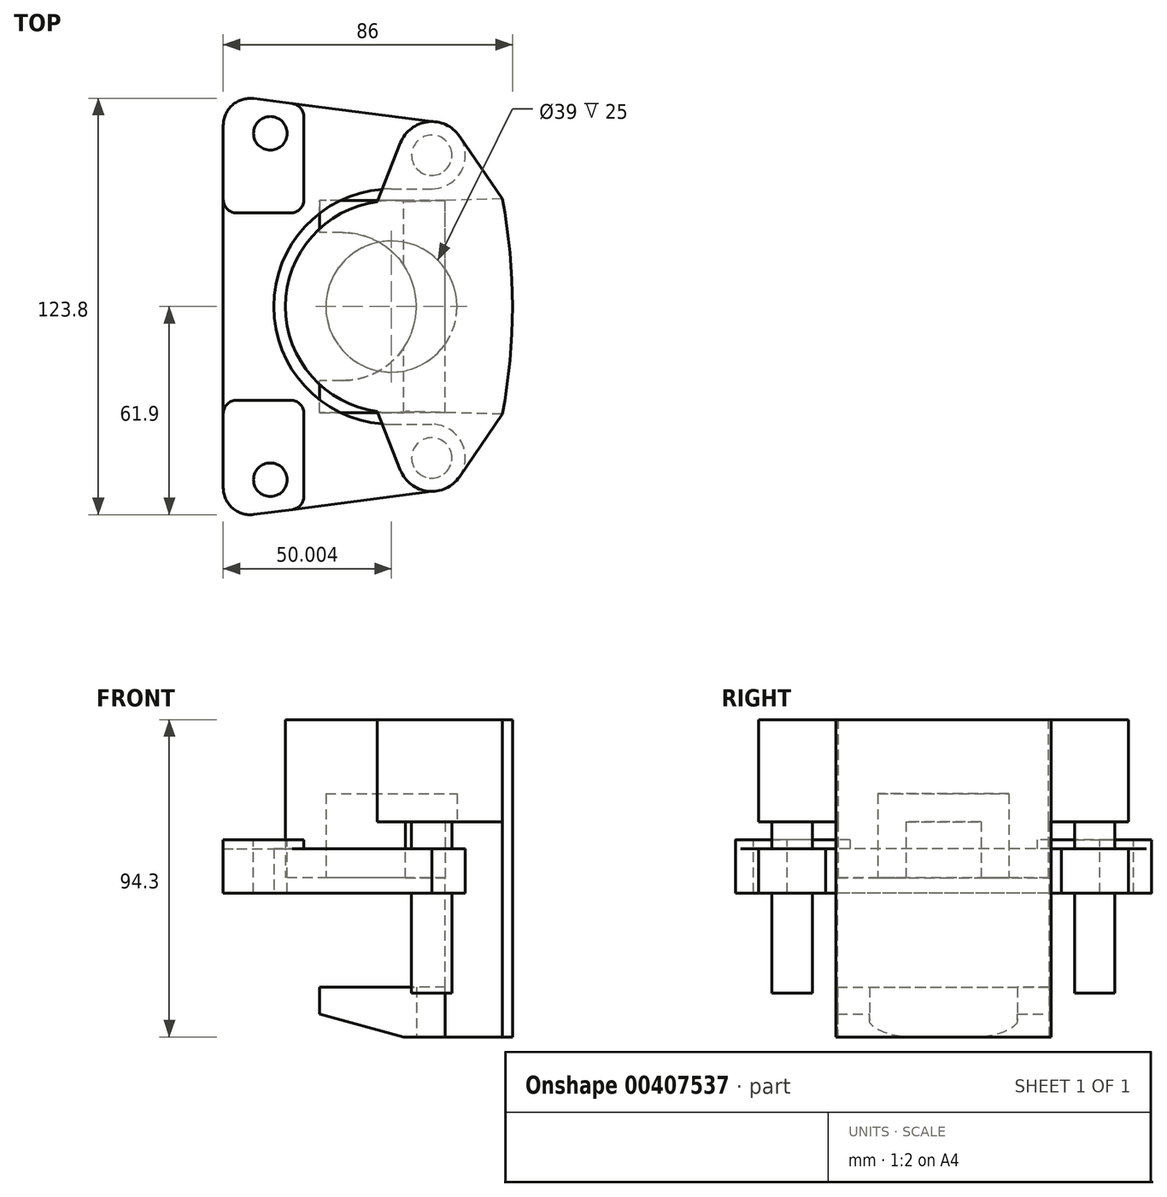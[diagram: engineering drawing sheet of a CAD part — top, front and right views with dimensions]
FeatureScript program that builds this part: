
annotation { "Feature Type Name" : "Feature", "Feature Type Description" : "" }
export const myFeature = defineFeature(function(context is Context, id is Id, definition is map)
    precondition{}
    {
        {
            var Q0;
            Q0=qCreatedBy(makeId("Top.planeOp"),FACE);
            var sketch = newSketch(context, id + "F0", { "sketchPlane" : qUnion([Q0])});
            skLineSegment(sketch, "E0", {"start": v(-41.04, 0) * mm, "end": v(-41.04, -63) * mm});
            skLineSegment(sketch, "E1", {"start": v(-41.04, -63) * mm, "end": v(20.96, -55) * mm});
            skLineSegment(sketch, "E2", {"start": v(20.96, -55) * mm, "end": v(20.96, -55) * mm});
            skArc(sketch, "E3", {"start": v(20.96, -55) * mm, "mid": v(30.96, -45) * mm, "end": v(20.96, -35) * mm});
            skLineSegment(sketch, "E4", {"start": v(20.96, -55) * mm, "end": v(20.96, -22.35) * mm, "construction": true});
            skLineSegment(sketch, "E5", {"start": v(-26.04, 0) * mm, "end": v(-26.04, 35.16) * mm, "construction": true});
            skArc(sketch, "E6", {"start": v(-26.04, 0) * mm, "mid": v(-15.79, -24.75) * mm, "end": v(8.96, -35) * mm});
            skLineSegment(sketch, "E7", {"start": v(8.96, -35) * mm, "end": v(20.96, -35) * mm});
            skLineSegment(sketch, "E8.MirrorCS", {"start": v(-41.04, 0) * mm, "end": v(-41.04, 63) * mm});
            skLineSegment(sketch, "E9.MirrorCS", {"start": v(-41.04, 63) * mm, "end": v(20.96, 55) * mm});
            skArc(sketch, "E10.MirrorCS", {"start": v(20.96, 55) * mm, "mid": v(30.96, 45) * mm, "end": v(20.96, 35) * mm});
            skLineSegment(sketch, "E11.MirrorCS", {"start": v(8.96, 35) * mm, "end": v(20.96, 35) * mm});
            skArc(sketch, "E12.MirrorCS", {"start": v(-26.04, 0) * mm, "mid": v(-15.79, 24.75) * mm, "end": v(8.96, 35) * mm});
            skSolve(sketch);
        }
        {
            var Q0;
            Q0=qSketchRegion(id+"F0",true);
            extrude(context, id + "F1", {"entities" : qUnion([Q0]), "depth" : 13.2 * mm, "offsetDistance" : 25 * mm});
        }
        {
            var Q0;
            Q0=makeQuery(id+"F1.opExtrude","SWEPT_EDGE",EDGE,{"disambiguationData":[OSD([sQuery(id+"F0.wireOp",EDGE,"E0"),sQuery(id+"F0.wireOp",EDGE,"E1")])]});
            var Q1;
            Q1=makeQuery(id+"F1.opExtrude","SWEPT_EDGE",EDGE,{"disambiguationData":[OSD([sQuery(id+"F0.wireOp",EDGE,"E8.MirrorCS"),sQuery(id+"F0.wireOp",EDGE,"E9.MirrorCS")])]});
            fillet(context, id + "F2", {"entities" : qUnion([Q0, Q1]), "tangentPropagation" : true, "radius" : 8 * mm, "defaultsChanged" : false, "vertexSettings" : [], "allowEdgeOverflow" : false});
        }
        {
            var Q0;
            Q0=makeQuery(id+"F1.opExtrude","CAP_FACE",FACE,{"disambiguationData":[OSD([sQuery(id+"F0.wireOp",EDGE,"E0"),sQuery(id+"F0.wireOp",EDGE,"E1"),sQuery(id+"F0.wireOp",EDGE,"E3"),sQuery(id+"F0.wireOp",EDGE,"E6"),sQuery(id+"F0.wireOp",EDGE,"E7"),sQuery(id+"F0.wireOp",EDGE,"E8.MirrorCS"),sQuery(id+"F0.wireOp",EDGE,"E9.MirrorCS"),sQuery(id+"F0.wireOp",EDGE,"E10.MirrorCS"),sQuery(id+"F0.wireOp",EDGE,"E11.MirrorCS"),sQuery(id+"F0.wireOp",EDGE,"E12.MirrorCS")])],"isStart":false});
            var sketch = newSketch(context, id + "F3", { "sketchPlane" : qUnion([Q0])});
            skLineSegment(sketch, "E13", {"start": v(-41.04, 53.9) * mm, "end": v(-41.04, 31.84) * mm});
            skLineSegment(sketch, "E14", {"start": v(-37.04, 27.84) * mm, "end": v(-21.04, 27.84) * mm});
            skLineSegment(sketch, "E15", {"start": v(-17.04, 31.84) * mm, "end": v(-17.04, 56.39) * mm});
            skLineSegment(sketch, "E16", {"start": v(-20.52, 60.35) * mm, "end": v(-32.01, 61.84) * mm});
            skArc(sketch, "E17", {"start": v(-32.01, 61.84) * mm, "mid": v(-38.32, 59.9) * mm, "end": v(-41.04, 53.9) * mm});
            skPoint(sketch, "E18.visualSharp", {"position": v(-17.04, 27.84) * mm});
            skArc(sketch, "E18.filletArc", {"start": v(-21.04, 27.84) * mm, "mid": v(-18.2, 29) * mm, "end": v(-17.04, 31.84) * mm});
            skPoint(sketch, "E19.visualSharp", {"position": v(-17.04, 59.9) * mm});
            skArc(sketch, "E19.filletArc", {"start": v(-17.04, 56.39) * mm, "mid": v(-18.03, 59.03) * mm, "end": v(-20.52, 60.35) * mm});
            skPoint(sketch, "E20.visualSharp", {"position": v(-41.04, 27.84) * mm});
            skArc(sketch, "E20.filletArc", {"start": v(-41.04, 31.84) * mm, "mid": v(-39.86, 29) * mm, "end": v(-37.04, 27.84) * mm});
            skLineSegment(sketch, "E21.MirrorCS", {"start": v(-20.52, -60.35) * mm, "end": v(-32.01, -61.84) * mm});
            skArc(sketch, "E22.MirrorCS", {"start": v(-21.04, -27.84) * mm, "mid": v(-18.2, -29) * mm, "end": v(-17.04, -31.84) * mm});
            skArc(sketch, "E23.MirrorCS", {"start": v(-41.04, -31.84) * mm, "mid": v(-39.86, -29) * mm, "end": v(-37.04, -27.84) * mm});
            skArc(sketch, "E24.MirrorCS", {"start": v(-32.01, -61.84) * mm, "mid": v(-38.32, -59.9) * mm, "end": v(-41.04, -53.9) * mm});
            skArc(sketch, "E25.MirrorCS", {"start": v(-17.04, -56.39) * mm, "mid": v(-18.03, -59.03) * mm, "end": v(-20.52, -60.35) * mm});
            skLineSegment(sketch, "E26.MirrorCS", {"start": v(-37.04, -27.84) * mm, "end": v(-21.04, -27.84) * mm});
            skLineSegment(sketch, "E27.MirrorCS", {"start": v(-41.04, -53.9) * mm, "end": v(-41.04, -31.84) * mm});
            skLineSegment(sketch, "E28.MirrorCS", {"start": v(-17.04, -31.84) * mm, "end": v(-17.04, -56.39) * mm});
            skPoint(sketch, "E29.MirrorP", {"position": v(-17.04, -59.9) * mm});
            skPoint(sketch, "E30.MirrorP", {"position": v(-17.04, -27.84) * mm});
            skPoint(sketch, "E31.MirrorP", {"position": v(-41.04, -27.84) * mm});
            skSolve(sketch);
        }
        {
            var Q0;
            Q0=qSketchRegion(id+"F3",true);
            extrude(context, id + "F4", {"entities" : qUnion([Q0]), "operationType" : NewBodyOperationType.ADD, "depth" : 2.6 * mm, "offsetDistance" : 25 * mm});
        }
        {
            var Q0;
            Q0=makeQuery(id+"F4.opExtrude","CAP_FACE",FACE,{"disambiguationData":[OSD([sQuery(id+"F3.wireOp",EDGE,"E13"),sQuery(id+"F3.wireOp",EDGE,"E14"),sQuery(id+"F3.wireOp",EDGE,"E15"),sQuery(id+"F3.wireOp",EDGE,"E16"),sQuery(id+"F3.wireOp",EDGE,"E17"),sQuery(id+"F3.wireOp",EDGE,"E18.filletArc"),sQuery(id+"F3.wireOp",EDGE,"E19.filletArc"),sQuery(id+"F3.wireOp",EDGE,"E20.filletArc")])],"isStart":false});
            var sketch = newSketch(context, id + "F5", { "sketchPlane" : qUnion([Q0])});
            skCircle(sketch, "E32", {"center": v(-27.04, 51.5) * mm, "radius": 5 * mm});
            skCircle(sketch, "E33.MirrorC", {"center": v(-27.04, -51.5) * mm, "radius": 5 * mm});
            skSolve(sketch);
        }
        {
            var Q0;
            Q0=qSketchRegion(id+"F5",true);
            extrude(context, id + "F6", {"entities" : qUnion([Q0]), "operationType" : NewBodyOperationType.REMOVE, "endBound" : BoundingType.THROUGH_ALL, "oppositeDirection" : true, "depth" : 25 * mm, "offsetDistance" : 25 * mm});
        }
        {
            var Q0;
            Q0=makeQuery(id+"F1.opExtrude","CAP_FACE",FACE,{"disambiguationData":[OSD([sQuery(id+"F0.wireOp",EDGE,"E0"),sQuery(id+"F0.wireOp",EDGE,"E1"),sQuery(id+"F0.wireOp",EDGE,"E3"),sQuery(id+"F0.wireOp",EDGE,"E6"),sQuery(id+"F0.wireOp",EDGE,"E7"),sQuery(id+"F0.wireOp",EDGE,"E8.MirrorCS"),sQuery(id+"F0.wireOp",EDGE,"E9.MirrorCS"),sQuery(id+"F0.wireOp",EDGE,"E10.MirrorCS"),sQuery(id+"F0.wireOp",EDGE,"E11.MirrorCS"),sQuery(id+"F0.wireOp",EDGE,"E12.MirrorCS")])],"isStart":false});
            var sketch = newSketch(context, id + "F7", { "sketchPlane" : qUnion([Q0])});
            skCircle(sketch, "E34", {"center": v(20.96, 45) * mm, "radius": 6 * mm});
            skCircle(sketch, "E35.MirrorC", {"center": v(20.96, -45) * mm, "radius": 6 * mm});
            skSolve(sketch);
        }
        {
            var Q0;
            Q0 = qSketchRegion(id + "F7", true);
            extrude(context, id + "F8", {"entities" : qUnion([Q0]), "operationType" : NewBodyOperationType.REMOVE, "oppositeDirection" : true, "depth" : 25 * mm, "offsetDistance" : 25 * mm});
        }
        {
            var Q0;
            Q0=qCreatedBy(makeId("Top.planeOp"),FACE);
            var sketch = newSketch(context, id + "F9", { "sketchPlane" : qUnion([Q0])});
            skCircle(sketch, "E36", {"center": v(8.96, 0) * mm, "radius": 31.5 * mm});
            skSolve(sketch);
        }
        {
            var Q0;
            Q0 = qSketchRegion(id + "F9", true);
            extrude(context, id + "F10", {"entities" : qUnion([Q0]), "depth" : 51.5 * mm, "offsetDistance" : 25 * mm, "hasSecondDirection" : true, "secondDirectionOppositeDirection" : false, "secondDirectionDepth" : 4.5 * mm});
        }
        {
            var Q0;
            Q0=makeQuery(id+"F10.opExtrude","CAP_FACE",FACE,{"disambiguationData":[OSD([sQuery(id+"F9.wireOp",EDGE,"E36")])],"isStart":false});
            var sketch = newSketch(context, id + "F11", { "sketchPlane" : qUnion([Q0])});
            skCircle(sketch, "E37", {"center": v(20.96, -45) * mm, "radius": 10 * mm});
            skLineSegment(sketch, "E38", {"start": v(11.66, -48.66) * mm, "end": v(4.8, -31.22) * mm});
            skArc(sketch, "E39", {"start": v(41.96, -32) * mm, "mid": v(44.21, -16.07) * mm, "end": v(44.96, 0) * mm});
            skLineSegment(sketch, "E40", {"start": v(-22.54, 0) * mm, "end": v(40.46, 0) * mm, "construction": true});
            skPoint(sketch, "E41", {"position": v(8.96, 0) * mm});
            skLineSegment(sketch, "E42", {"start": v(41.96, -32) * mm, "end": v(29.22, -50.64) * mm});
            skCircle(sketch, "E43.MirrorC", {"center": v(20.96, 45) * mm, "radius": 10 * mm});
            skLineSegment(sketch, "E44.MirrorCS", {"start": v(11.66, 48.66) * mm, "end": v(4.8, 31.22) * mm});
            skLineSegment(sketch, "E45.MirrorCS", {"start": v(41.96, 32) * mm, "end": v(29.22, 50.64) * mm});
            skArc(sketch, "E46.MirrorCS", {"start": v(41.96, 32) * mm, "mid": v(44.21, 16.07) * mm, "end": v(44.96, 0) * mm});
            skLineSegment(sketch, "E47", {"start": v(4.8, -31.22) * mm, "end": v(4.8, 0) * mm});
            skLineSegment(sketch, "E48", {"start": v(4.8, 0) * mm, "end": v(4.8, 31.22) * mm});
            skSolve(sketch);
        }
        {
            var Q0;
            Q0 = qSketchRegion(id + "F11", true);
            var Q1;
            Q1=makeQuery(id+"F1.opExtrude","CAP_FACE",FACE,{"disambiguationData":[OSD([sQuery(id+"F0.wireOp",EDGE,"E0"),sQuery(id+"F0.wireOp",EDGE,"E1"),sQuery(id+"F0.wireOp",EDGE,"E3"),sQuery(id+"F0.wireOp",EDGE,"E6"),sQuery(id+"F0.wireOp",EDGE,"E7"),sQuery(id+"F0.wireOp",EDGE,"E8.MirrorCS"),sQuery(id+"F0.wireOp",EDGE,"E9.MirrorCS"),sQuery(id+"F0.wireOp",EDGE,"E10.MirrorCS"),sQuery(id+"F0.wireOp",EDGE,"E11.MirrorCS"),sQuery(id+"F0.wireOp",EDGE,"E12.MirrorCS")])],"isStart":false});
            extrude(context, id + "F12", {"entities" : qUnion([Q0]), "operationType" : NewBodyOperationType.ADD, "endBound" : BoundingType.UP_TO_SURFACE, "oppositeDirection" : true, "depth" : 25 * mm, "endBoundEntityFace" : qUnion([Q1]), "hasOffset" : true, "offsetDistance" : 8 * mm});
        }
        {
            var Q0;
            Q0=makeQuery(id+"F10.opExtrude","CAP_FACE",FACE,{"disambiguationData":[OSD([sQuery(id+"F9.wireOp",EDGE,"E36")])],"isStart":true});
            var sketch = newSketch(context, id + "F13", { "sketchPlane" : qUnion([Q0])});
            skCircle(sketch, "E49", {"center": v(8.96, 0) * mm, "radius": 19.5 * mm});
            skSolve(sketch);
        }
        {
            var Q0;
            Q0 = qSketchRegion(id + "F13", true);
            extrude(context, id + "F14", {"entities" : qUnion([Q0]), "operationType" : NewBodyOperationType.REMOVE, "oppositeDirection" : true, "depth" : 25 * mm, "offsetDistance" : 25 * mm});
        }
        {
            var Q0;
            Q0=makeQuery(id+"F12.opExtrude","CAP_FACE",FACE,{"disambiguationData":[OSD([sQuery(id+"F11.wireOp",EDGE,"E37"),sQuery(id+"F11.wireOp",EDGE,"E38"),sQuery(id+"F11.wireOp",EDGE,"E39"),sQuery(id+"F11.wireOp",EDGE,"E42"),sQuery(id+"F11.wireOp",EDGE,"E43.MirrorC"),sQuery(id+"F11.wireOp",EDGE,"E44.MirrorCS"),sQuery(id+"F11.wireOp",EDGE,"E45.MirrorCS"),sQuery(id+"F11.wireOp",EDGE,"E46.MirrorCS"),sQuery(id+"F11.wireOp",EDGE,"E47"),sQuery(id+"F11.wireOp",EDGE,"E48")])],"isStart":false});
            var sketch = newSketch(context, id + "F15", { "sketchPlane" : qUnion([Q0])});
            skCircle(sketch, "E50", {"center": v(20.96, -45) * mm, "radius": 6 * mm});
            skCircle(sketch, "E51.MirrorC", {"center": v(20.96, 45) * mm, "radius": 6 * mm});
            skSolve(sketch);
        }
        {
            var Q0;
            Q0 = qSketchRegion(id + "F15", true);
            extrude(context, id + "F16", {"entities" : qUnion([Q0]), "operationType" : NewBodyOperationType.ADD, "depth" : 51 * mm, "offsetDistance" : 25 * mm});
        }
        {
            var Q0;
            Q0=makeQuery(id+"F12.opExtrude","CAP_FACE",FACE,{"disambiguationData":[OSD([sQuery(id+"F11.wireOp",EDGE,"E37"),sQuery(id+"F11.wireOp",EDGE,"E38"),sQuery(id+"F11.wireOp",EDGE,"E39"),sQuery(id+"F11.wireOp",EDGE,"E42"),sQuery(id+"F11.wireOp",EDGE,"E43.MirrorC"),sQuery(id+"F11.wireOp",EDGE,"E44.MirrorCS"),sQuery(id+"F11.wireOp",EDGE,"E45.MirrorCS"),sQuery(id+"F11.wireOp",EDGE,"E46.MirrorCS"),sQuery(id+"F11.wireOp",EDGE,"E47"),sQuery(id+"F11.wireOp",EDGE,"E48")])],"isStart":false});
            var sketch = newSketch(context, id + "F17", { "sketchPlane" : qUnion([Q0])});
            skArc(sketch, "E52", {"start": v(41.96, -32) * mm, "mid": v(44.21, -16.07) * mm, "end": v(44.96, 0) * mm});
            skLineSegment(sketch, "E53", {"start": v(41.96, -32) * mm, "end": v(13.13, -31.22) * mm});
            skLineSegment(sketch, "E54", {"start": v(13.13, -31.22) * mm, "end": v(13.13, -31.22) * mm});
            skLineSegment(sketch, "E55", {"start": v(13.13, -31.22) * mm, "end": v(32.09, 0) * mm});
            skLineSegment(sketch, "E56.MirrorCS", {"start": v(13.13, 31.22) * mm, "end": v(32.09, 0) * mm});
            skLineSegment(sketch, "E57.MirrorCS", {"start": v(41.96, 32) * mm, "end": v(13.13, 31.22) * mm});
            skArc(sketch, "E58.MirrorCS", {"start": v(41.96, 32) * mm, "mid": v(44.21, 16.07) * mm, "end": v(44.96, 0) * mm});
            skSolve(sketch);
        }
        {
            var Q0;
            Q0 = qSketchRegion(id + "F17", true);
            var Q1;
            Q1=makeQuery(id+"F10.opExtrude","CAP_FACE",FACE,{"disambiguationData":[OSD([sQuery(id+"F9.wireOp",EDGE,"E36")])],"isStart":true});
            extrude(context, id + "F18", {"entities" : qUnion([Q0]), "operationType" : NewBodyOperationType.ADD, "endBound" : BoundingType.UP_TO_SURFACE, "depth" : 25 * mm, "endBoundEntityFace" : qUnion([Q1]), "offsetDistance" : 25 * mm});
        }
        {
            var Q0;
            {var subQ0=sQuery(id+"F11.wireOp",EDGE,"E46.MirrorCS");var subQ1=sQuery(id+"F11.wireOp",EDGE,"E39");var subQ2=sQuery(id+"F11.wireOp",EDGE,"E38");var subQ3=sQuery(id+"F11.wireOp",EDGE,"E37");var subQ4=sQuery(id+"F11.wireOp",EDGE,"E42");Q0=makeQuery(id+"F18.boolean.opBoolean","SPLIT",FACE,{"disambiguationData":[TD([makeQuery(id+"F12.opExtrude","SWEPT_FACE",FACE,{"disambiguationData":[OSD([subQ3])]})])],"derivedFrom":makeQuery(id+"F12.opExtrude","CAP_FACE",FACE,{"disambiguationData":[OSD([subQ3,subQ2,subQ1,subQ4,sQuery(id+"F11.wireOp",EDGE,"E43.MirrorC"),sQuery(id+"F11.wireOp",EDGE,"E44.MirrorCS"),sQuery(id+"F11.wireOp",EDGE,"E45.MirrorCS"),subQ0,sQuery(id+"F11.wireOp",EDGE,"E47"),sQuery(id+"F11.wireOp",EDGE,"E48")])],"isStart":false})});}
            var sketch = newSketch(context, id + "F19", { "sketchPlane" : qUnion([Q0])});
            skArc(sketch, "E59", {"start": v(41.96, -32) * mm, "mid": v(44.21, -16.07) * mm, "end": v(44.96, 0) * mm});
            skLineSegment(sketch, "E60", {"start": v(41.96, -32) * mm, "end": v(24.97, -31.54) * mm});
            skArc(sketch, "E61.MirrorCS", {"start": v(41.96, 32) * mm, "mid": v(44.21, 16.07) * mm, "end": v(44.96, 0) * mm});
            skLineSegment(sketch, "E62.MirrorCS", {"start": v(41.96, 32) * mm, "end": v(24.97, 31.54) * mm});
            skLineSegment(sketch, "E63", {"start": v(24.97, 31.54) * mm, "end": v(24.97, -31.54) * mm});
            skSolve(sketch);
        }
        {
            var Q0;
            Q0 = qSketchRegion(id + "F19", true);
            extrude(context, id + "F20", {"entities" : qUnion([Q0]), "operationType" : NewBodyOperationType.ADD, "depth" : 64 * mm, "offsetDistance" : 25 * mm});
        }
        {
            var Q0;
            Q0=makeQuery(id+"F20.opExtrude","CAP_FACE",FACE,{"disambiguationData":[OSD([sQuery(id+"F19.wireOp",EDGE,"E59"),sQuery(id+"F19.wireOp",EDGE,"E60"),sQuery(id+"F19.wireOp",EDGE,"E61.MirrorCS"),sQuery(id+"F19.wireOp",EDGE,"E62.MirrorCS"),sQuery(id+"F19.wireOp",EDGE,"E63")])],"isStart":false});
            var sketch = newSketch(context, id + "F21", { "sketchPlane" : qUnion([Q0])});
            skLineSegment(sketch, "E64", {"start": v(24.97, 31.54) * mm, "end": v(-12.34, 31.54) * mm});
            skLineSegment(sketch, "E65", {"start": v(-12.34, 31.54) * mm, "end": v(-12.34, 22) * mm});
            skLineSegment(sketch, "E66", {"start": v(-12.34, 22) * mm, "end": v(-5.59, 22) * mm});
            skArc(sketch, "E67", {"start": v(16.41, 0) * mm, "mid": v(9.97, 15.56) * mm, "end": v(-5.59, 22) * mm});
            skLineSegment(sketch, "E68", {"start": v(24.97, 31.54) * mm, "end": v(24.97, 0) * mm});
            skLineSegment(sketch, "E69.MirrorCS", {"start": v(24.97, -31.54) * mm, "end": v(-12.34, -31.54) * mm});
            skArc(sketch, "E70.MirrorCS", {"start": v(16.41, 0) * mm, "mid": v(9.97, -15.56) * mm, "end": v(-5.59, -22) * mm});
            skLineSegment(sketch, "E71.MirrorCS", {"start": v(24.97, -31.54) * mm, "end": v(24.97, 0) * mm});
            skLineSegment(sketch, "E72.MirrorCS", {"start": v(-12.34, -22) * mm, "end": v(-5.59, -22) * mm});
            skLineSegment(sketch, "E73.MirrorCS", {"start": v(-12.34, -31.54) * mm, "end": v(-12.34, -22) * mm});
            skSolve(sketch);
        }
        {
            var Q0;
            Q0 = qSketchRegion(id + "F21", true);
            var Q1;
            Q1=makeQuery(id+"F1.opExtrude","CAP_FACE",FACE,{"disambiguationData":[OSD([sQuery(id+"F0.wireOp",EDGE,"E0"),sQuery(id+"F0.wireOp",EDGE,"E1"),sQuery(id+"F0.wireOp",EDGE,"E3"),sQuery(id+"F0.wireOp",EDGE,"E6"),sQuery(id+"F0.wireOp",EDGE,"E7"),sQuery(id+"F0.wireOp",EDGE,"E8.MirrorCS"),sQuery(id+"F0.wireOp",EDGE,"E9.MirrorCS"),sQuery(id+"F0.wireOp",EDGE,"E10.MirrorCS"),sQuery(id+"F0.wireOp",EDGE,"E11.MirrorCS"),sQuery(id+"F0.wireOp",EDGE,"E12.MirrorCS")])],"isStart":true});
            extrude(context, id + "F22", {"entities" : qUnion([Q0]), "operationType" : NewBodyOperationType.ADD, "endBound" : BoundingType.UP_TO_SURFACE, "oppositeDirection" : true, "depth" : 25 * mm, "endBoundEntityFace" : qUnion([Q1]), "hasOffset" : true, "offsetDistance" : 28 * mm});
        }
        {
            var Q0;
            Q0=makeQuery(id+"F22.opExtrude","SWEPT_FACE",FACE,{"disambiguationData":[OSD([sQuery(id+"F21.wireOp",EDGE,"E69.MirrorCS")])]});
            var sketch = newSketch(context, id + "F23", { "sketchPlane" : qUnion([Q0])});
            skLineSegment(sketch, "E74", {"start": v(12.34, -36) * mm, "end": v(12.34, -42.8) * mm});
            skLineSegment(sketch, "E75", {"start": v(12.34, -42.8) * mm, "end": v(-12.66, -42.8) * mm});
            skLineSegment(sketch, "E76", {"start": v(-12.66, -42.8) * mm, "end": v(12.34, -36) * mm});
            skSolve(sketch);
        }
        {
            var Q0;
            Q0 = qSketchRegion(id + "F23", true);
            extrude(context, id + "F24", {"entities" : qUnion([Q0]), "operationType" : NewBodyOperationType.REMOVE, "endBound" : BoundingType.THROUGH_ALL, "oppositeDirection" : true, "depth" : 25 * mm, "offsetDistance" : 25 * mm});
        }
    });
